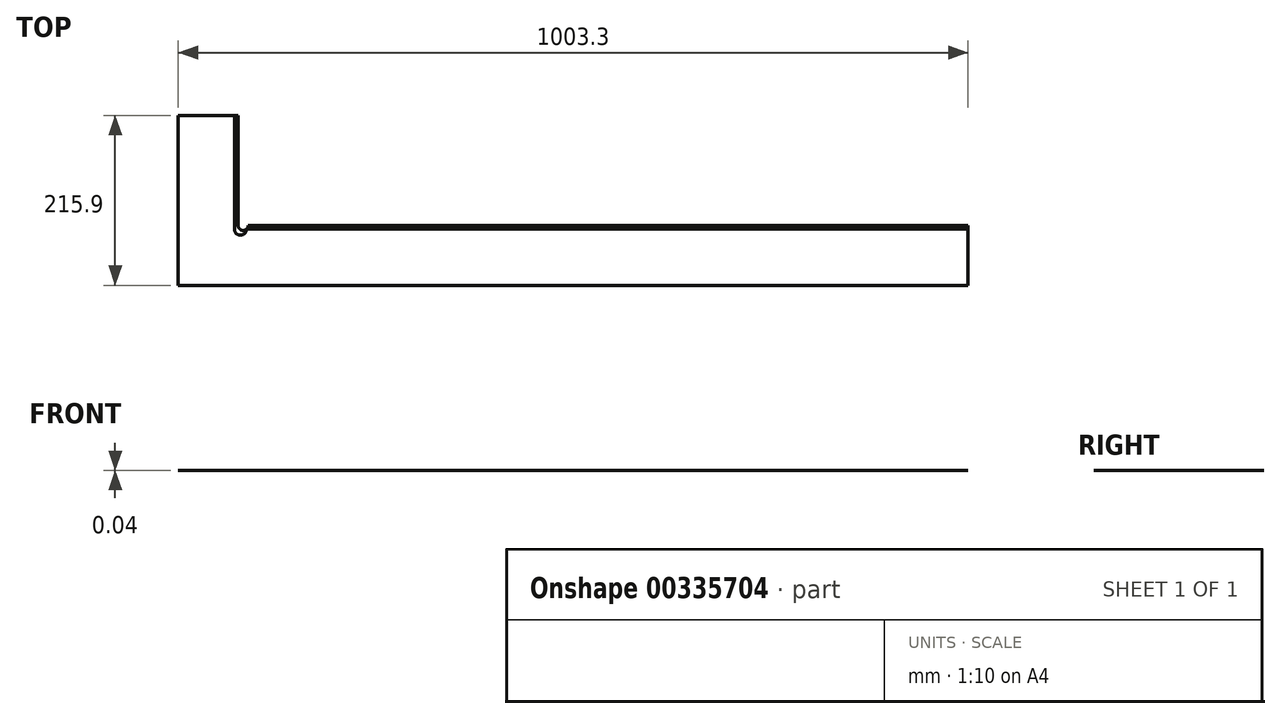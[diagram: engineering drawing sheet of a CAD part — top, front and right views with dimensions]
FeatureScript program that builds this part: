
annotation { "Feature Type Name" : "Feature", "Feature Type Description" : "" }
export const myFeature = defineFeature(function(context is Context, id is Id, definition is map)
    precondition{}
    {
        {
            var Q0;
            Q0=qCreatedBy(makeId("Top.planeOp"),FACE);
            var sketch = newSketch(context, id + "F0", { "sketchPlane" : qUnion([Q0])});
            skPoint(sketch, "E0.0", {"position": v(0, 0) * mm});
            skPoint(sketch, "E1.0", {"position": v(-4.76, -4.76) * mm});
            skPoint(sketch, "E2.0", {"position": v(0, 139.7) * mm});
            skLineSegment(sketch, "E3", {"start": v(12.7, 0) * mm, "end": v(927.1, 0) * mm});
            skLineSegment(sketch, "E4", {"start": v(927.1, 0) * mm, "end": v(927.1, -76.2) * mm});
            skLineSegment(sketch, "E5", {"start": v(927.1, -76.2) * mm, "end": v(-76.2, -76.2) * mm});
            skLineSegment(sketch, "E6", {"start": v(-76.2, -76.2) * mm, "end": v(-76.2, 139.7) * mm});
            skLineSegment(sketch, "E7", {"start": v(-76.2, 139.7) * mm, "end": v(0, 139.7) * mm});
            skLineSegment(sketch, "E8", {"start": v(0, 139.7) * mm, "end": v(0, 0) * mm});
            skLineSegment(sketch, "E9", {"start": v(-4.76, -4.76) * mm, "end": v(-4.76, 139.7) * mm});
            skArc(sketch, "E10", {"start": v(0, 0) * mm, "mid": v(6.35, -6.35) * mm, "end": v(12.7, 0) * mm});
            skArc(sketch, "E11", {"start": v(-4.76, -4.76) * mm, "mid": v(2.9, -12.42) * mm, "end": v(10.55, -4.76) * mm});
            skLineSegment(sketch, "E12.trimOffspring", {"start": v(10.55, -4.76) * mm, "end": v(927.1, -4.76) * mm});
            skSolve(sketch);
        }
        {
            var Q0;
            {var subQ4=sQuery(id+"F0.wireOp",EDGE,"E3");Q0=makeQuery(id+"F0.imprint","IMPRINT",FACE,{"disambiguationData":[TD([[makeQuery(id+"F0.imprint","IMPRINT",EDGE,{"derivedFrom":subQ4}),-1.0]])]});}
            var Q1;
            {var subQ3=sQuery(id+"F0.wireOp",EDGE,"E5");Q1=makeQuery(id+"F0.imprint","IMPRINT",FACE,{"disambiguationData":[TD([[makeQuery(id+"F0.imprint","IMPRINT",EDGE,{"derivedFrom":subQ3}),-1.0]])]});}
            var Q2;
            {var subQ1=sQuery(id+"F0.wireOp",EDGE,"E8");Q2=makeQuery(id+"F0.imprint","IMPRINT",FACE,{"disambiguationData":[TD([[makeQuery(id+"F0.imprint","IMPRINT",EDGE,{"derivedFrom":subQ1}),-1.0]])]});}
            extrude(context, id + "F1", {"entities" : qUnion([Q0, Q1, Q2]), "oppositeDirection" : true, "depth" : 3 / 101.6 * mm});
        }
        {
            var Q0;
            {var subQ3=sQuery(id+"F0.wireOp",EDGE,"E5");Q0=makeQuery(id+"F0.imprint","IMPRINT",FACE,{"disambiguationData":[TD([[makeQuery(id+"F0.imprint","IMPRINT",EDGE,{"derivedFrom":subQ3}),-1.0]])]});}
            extrude(context, id + "F2", {"entities" : qUnion([Q0]), "operationType" : NewBodyOperationType.ADD, "depth" : 1 / 101.6 * mm});
        }
    });
